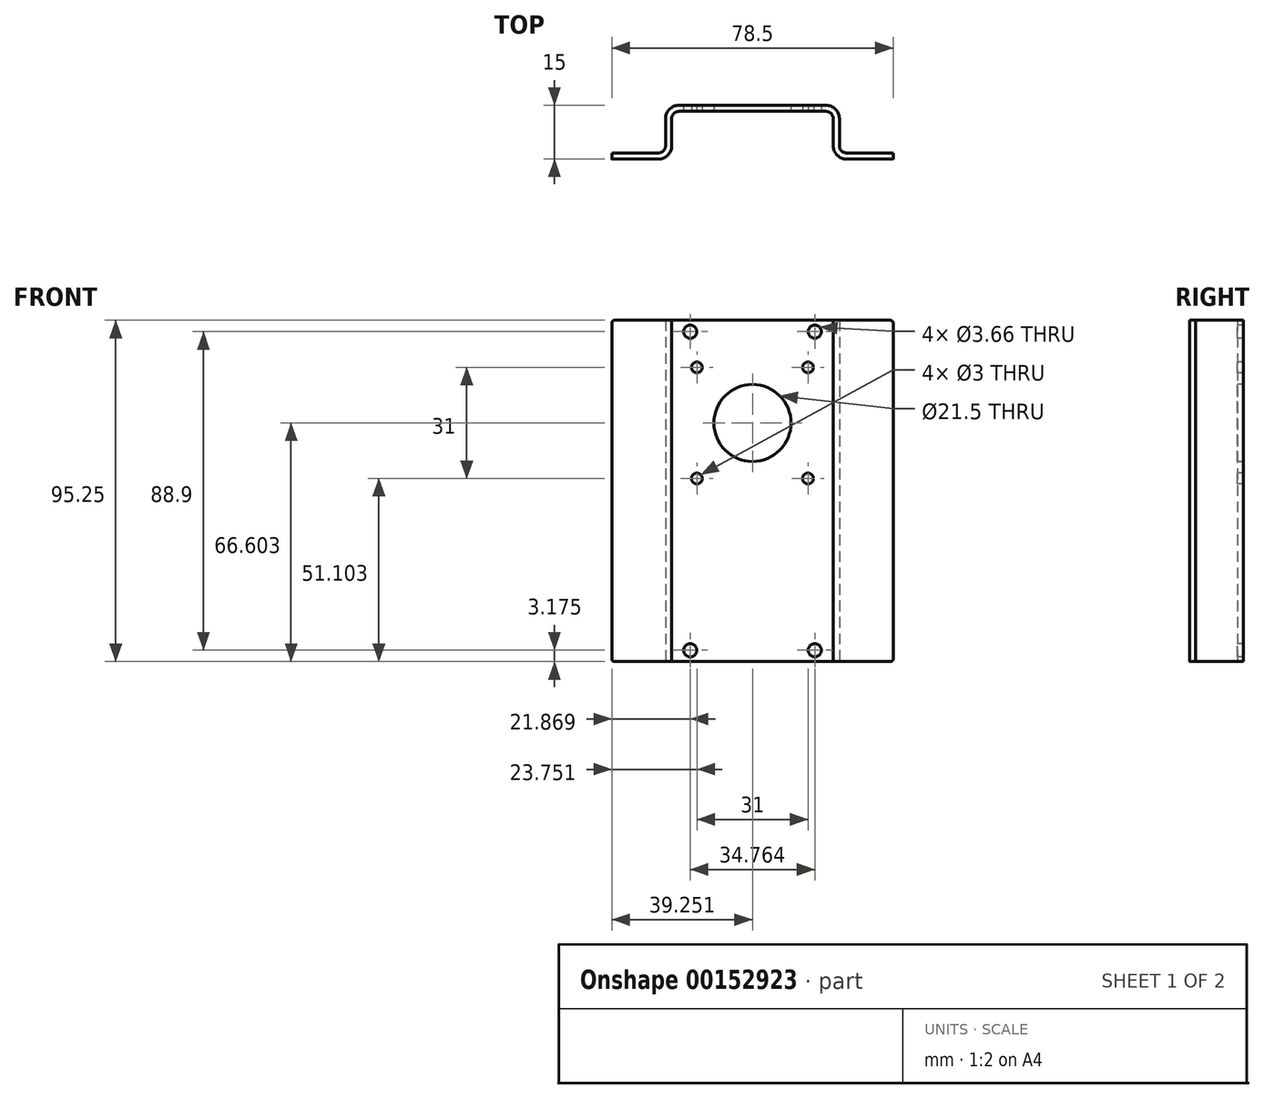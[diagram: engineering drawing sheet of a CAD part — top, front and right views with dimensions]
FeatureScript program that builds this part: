
annotation { "Feature Type Name" : "Feature", "Feature Type Description" : "" }
export const myFeature = defineFeature(function(context is Context, id is Id, definition is map)
    precondition{}
    {
        {
            var Q0;
            Q0=qCreatedBy(makeId("Top.planeOp"),FACE);
            var sketch = newSketch(context, id + "F0", { "sketchPlane" : qUnion([Q0])});
            skLineSegment(sketch, "E0.left", {"start": v(0, 0) * mm, "end": v(0, -13.3) * mm});
            skLineSegment(sketch, "E0.right", {"start": v(-1.7, 1.7) * mm, "end": v(-1.7, -11.58) * mm});
            skLineSegment(sketch, "E1.bottom", {"start": v(-1.7, -11.58) * mm, "end": v(-16.7, -11.58) * mm});
            skLineSegment(sketch, "E1.top", {"start": v(0, -13.3) * mm, "end": v(-16.7, -13.3) * mm});
            skLineSegment(sketch, "E1.right", {"start": v(-16.7, -11.58) * mm, "end": v(-16.7, -13.3) * mm});
            skLineSegment(sketch, "E2.bottom", {"start": v(0, 0) * mm, "end": v(45.08, 0) * mm});
            skLineSegment(sketch, "E2.top", {"start": v(-1.7, 1.7) * mm, "end": v(46.8, 1.7) * mm});
            skLineSegment(sketch, "E3", {"start": v(0, -6.65) * mm, "end": v(-1.7, -6.65) * mm, "construction": true});
            skLineSegment(sketch, "E4.left", {"start": v(45.08, 0) * mm, "end": v(45.08, -13.3) * mm});
            skLineSegment(sketch, "E4.right", {"start": v(46.8, 1.7) * mm, "end": v(46.8, -11.58) * mm});
            skLineSegment(sketch, "E5.bottom", {"start": v(46.8, -11.58) * mm, "end": v(61.8, -11.58) * mm});
            skLineSegment(sketch, "E5.top", {"start": v(45.08, -13.3) * mm, "end": v(61.8, -13.3) * mm});
            skLineSegment(sketch, "E5.right", {"start": v(61.8, -11.58) * mm, "end": v(61.8, -13.3) * mm});
            skLineSegment(sketch, "E6", {"start": v(45.08, -6.65) * mm, "end": v(46.8, -6.65) * mm, "construction": true});
            skLineSegment(sketch, "E7", {"start": v(22.54, 0) * mm, "end": v(22.54, 1.7) * mm, "construction": true});
            skPoint(sketch, "E8", {"position": v(-9.2, -11.58) * mm});
            skPoint(sketch, "E9", {"position": v(54.3, -11.58) * mm});
            skSolve(sketch);
        }
        {
            var Q0;
            Q0=qSketchRegion(id+"F0",true);
            extrude(context, id + "F1", {"entities" : qUnion([Q0]), "depth" : 95.25 * mm});
        }
        {
            var Q0;
            Q0=makeQuery(id+"F1.opExtrude","SWEPT_EDGE",EDGE,{"disambiguationData":[OSD([sQuery(id+"F0.wireOp",EDGE,"E0.left"),sQuery(id+"F0.wireOp",EDGE,"E2.bottom")])]});
            var Q1;
            Q1=makeQuery(id+"F1.opExtrude","SWEPT_EDGE",EDGE,{"disambiguationData":[OSD([sQuery(id+"F0.wireOp",EDGE,"E0.right"),sQuery(id+"F0.wireOp",EDGE,"E1.bottom")])]});
            var Q2;
            Q2=makeQuery(id+"F1.opExtrude","SWEPT_EDGE",EDGE,{"disambiguationData":[OSD([sQuery(id+"F0.wireOp",EDGE,"E2.bottom"),sQuery(id+"F0.wireOp",EDGE,"E4.left")])]});
            var Q3;
            Q3=makeQuery(id+"F1.opExtrude","SWEPT_EDGE",EDGE,{"disambiguationData":[OSD([sQuery(id+"F0.wireOp",EDGE,"E4.right"),sQuery(id+"F0.wireOp",EDGE,"E5.bottom")])]});
            fillet(context, id + "F2", {"entities" : qUnion([Q0, Q1, Q2, Q3]), "radius" : 1.98 * mm, "tangentPropagation" : true, "allowEdgeOverflow" : false});
        }
        {
            var Q0;
            Q0=makeQuery(id+"F1.opExtrude","SWEPT_EDGE",EDGE,{"disambiguationData":[OSD([sQuery(id+"F0.wireOp",EDGE,"E0.left"),sQuery(id+"F0.wireOp",EDGE,"E1.top")])]});
            var Q1;
            Q1=makeQuery(id+"F1.opExtrude","SWEPT_EDGE",EDGE,{"disambiguationData":[OSD([sQuery(id+"F0.wireOp",EDGE,"E0.right"),sQuery(id+"F0.wireOp",EDGE,"E2.top")])]});
            var Q2;
            Q2=makeQuery(id+"F1.opExtrude","SWEPT_EDGE",EDGE,{"disambiguationData":[OSD([sQuery(id+"F0.wireOp",EDGE,"E2.top"),sQuery(id+"F0.wireOp",EDGE,"E4.right")])]});
            var Q3;
            Q3=makeQuery(id+"F1.opExtrude","SWEPT_EDGE",EDGE,{"disambiguationData":[OSD([sQuery(id+"F0.wireOp",EDGE,"E4.left"),sQuery(id+"F0.wireOp",EDGE,"E5.top")])]});
            fillet(context, id + "F3", {"entities" : qUnion([Q0, Q1, Q2, Q3]), "radius" : 3.7 * mm, "tangentPropagation" : true, "allowEdgeOverflow" : false});
        }
        {
            var Q0;
            Q0=makeQuery(id+"F1.opExtrude","CAP_EDGE",EDGE,{"disambiguationData":[OSD([sQuery(id+"F0.wireOp",EDGE,"E1.right")])],"isStart":true});
            var Q1;
            Q1=makeQuery(id+"F1.opExtrude","CAP_EDGE",EDGE,{"disambiguationData":[OSD([sQuery(id+"F0.wireOp",EDGE,"E1.right")])],"isStart":false});
            var Q2;
            Q2=makeQuery(id+"F1.opExtrude","CAP_EDGE",EDGE,{"disambiguationData":[OSD([sQuery(id+"F0.wireOp",EDGE,"E5.right")])],"isStart":true});
            var Q3;
            Q3=makeQuery(id+"F1.opExtrude","CAP_EDGE",EDGE,{"disambiguationData":[OSD([sQuery(id+"F0.wireOp",EDGE,"E5.right")])],"isStart":false});
            fillet(context, id + "F4", {"entities" : qUnion([Q0, Q1, Q2, Q3]), "radius" : 0.76 * mm, "tangentPropagation" : true, "allowEdgeOverflow" : false});
        }
        {
            var Q0;
            Q0=makeQuery(id+"F1.opExtrude","SWEPT_FACE",FACE,{"disambiguationData":[OSD([sQuery(id+"F0.wireOp",EDGE,"E2.bottom")])]});
            var sketch = newSketch(context, id + "F5", { "sketchPlane" : qUnion([Q0])});
            skCircle(sketch, "E10", {"center": v(5.16, 92.08) * mm, "radius": 1.83 * mm});
            skCircle(sketch, "E11", {"center": v(5.16, 3.17) * mm, "radius": 1.83 * mm});
            skLineSegment(sketch, "E12", {"start": v(22.54, 0) * mm, "end": v(22.54, 95.25) * mm, "construction": true});
            skLineSegment(sketch, "E13", {"start": v(43.1, 92.08) * mm, "end": v(39.92, 92.08) * mm, "construction": true});
            skLineSegment(sketch, "E14", {"start": v(39.92, 92.08) * mm, "end": v(39.92, 95.25) * mm, "construction": true});
            skLineSegment(sketch, "E15.bottom", {"start": v(39.92, 92.08) * mm, "end": v(5.16, 92.08) * mm, "construction": true});
            skLineSegment(sketch, "E15.top", {"start": v(39.92, 3.17) * mm, "end": v(5.16, 3.17) * mm, "construction": true});
            skLineSegment(sketch, "E15.left", {"start": v(39.92, 92.08) * mm, "end": v(39.92, 3.18) * mm, "construction": true});
            skLineSegment(sketch, "E15.right", {"start": v(5.16, 92.08) * mm, "end": v(5.16, 3.17) * mm, "construction": true});
            skPoint(sketch, "E15.middle", {"position": v(22.54, 47.63) * mm});
            skCircle(sketch, "E16", {"center": v(39.92, 92.08) * mm, "radius": 1.83 * mm});
            skCircle(sketch, "E17", {"center": v(39.92, 3.18) * mm, "radius": 1.83 * mm});
            skSolve(sketch);
        }
        {
            var Q0;
            Q0=qSketchRegion(id+"F5",true);
            var Q1;
            Q1=makeQuery(id+"F1.opExtrude","SWEPT_FACE",FACE,{"disambiguationData":[OSD([sQuery(id+"F0.wireOp",EDGE,"E2.top")])]});
            extrude(context, id + "F6", {"entities" : qUnion([Q0]), "operationType" : NewBodyOperationType.REMOVE, "endBound" : BoundingType.UP_TO_SURFACE, "oppositeDirection" : true, "endBoundEntityFace" : qUnion([Q1]), "depth" : 25.4 * mm});
        }
        {
            var Q0;
            Q0=makeQuery(id+"F1.opExtrude","SWEPT_FACE",FACE,{"disambiguationData":[OSD([sQuery(id+"F0.wireOp",EDGE,"E2.bottom")])]});
            var sketch = newSketch(context, id + "F7", { "sketchPlane" : qUnion([Q0])});
            skLineSegment(sketch, "E18", {"start": v(22.54, 0) * mm, "end": v(22.54, 66.6) * mm, "construction": true});
            skLineSegment(sketch, "E19.bottom", {"start": v(38.04, 51.1) * mm, "end": v(7.04, 51.1) * mm, "construction": true});
            skLineSegment(sketch, "E19.top", {"start": v(38.04, 82.1) * mm, "end": v(7.04, 82.1) * mm, "construction": true});
            skLineSegment(sketch, "E19.left", {"start": v(38.04, 51.1) * mm, "end": v(38.04, 82.1) * mm, "construction": true});
            skLineSegment(sketch, "E19.right", {"start": v(7.04, 51.1) * mm, "end": v(7.04, 82.1) * mm, "construction": true});
            skPoint(sketch, "E19.middle", {"position": v(22.54, 66.6) * mm});
            skCircle(sketch, "E20", {"center": v(22.54, 66.6) * mm, "radius": 10.75 * mm});
            skCircle(sketch, "E21", {"center": v(38.04, 82.1) * mm, "radius": 1.5 * mm});
            skCircle(sketch, "E22", {"center": v(38.04, 51.1) * mm, "radius": 1.5 * mm});
            skCircle(sketch, "E23", {"center": v(7.04, 51.1) * mm, "radius": 1.5 * mm});
            skCircle(sketch, "E24", {"center": v(7.04, 82.1) * mm, "radius": 1.5 * mm});
            skLineSegment(sketch, "E25", {"start": v(22.54, 66.6) * mm, "end": v(22.54, 88.1) * mm, "construction": true});
            skLineSegment(sketch, "E26", {"start": v(22.54, 88.1) * mm, "end": v(39.92, 88.1) * mm, "construction": true});
            skLineSegment(sketch, "E27", {"start": v(39.92, 88.1) * mm, "end": v(39.92, 92.08) * mm, "construction": true});
            skSolve(sketch);
        }
        {
            var Q0;
            Q0 = qSketchRegion(id + "F7", true);
            var Q1;
            Q1=makeQuery(id+"F1.opExtrude","SWEPT_FACE",FACE,{"disambiguationData":[OSD([sQuery(id+"F0.wireOp",EDGE,"E2.top")])]});
            extrude(context, id + "F8", {"entities" : qUnion([Q0]), "operationType" : NewBodyOperationType.REMOVE, "endBound" : BoundingType.UP_TO_SURFACE, "oppositeDirection" : true, "endBoundEntityFace" : qUnion([Q1]), "depth" : 25.4 * mm});
        }
    });
